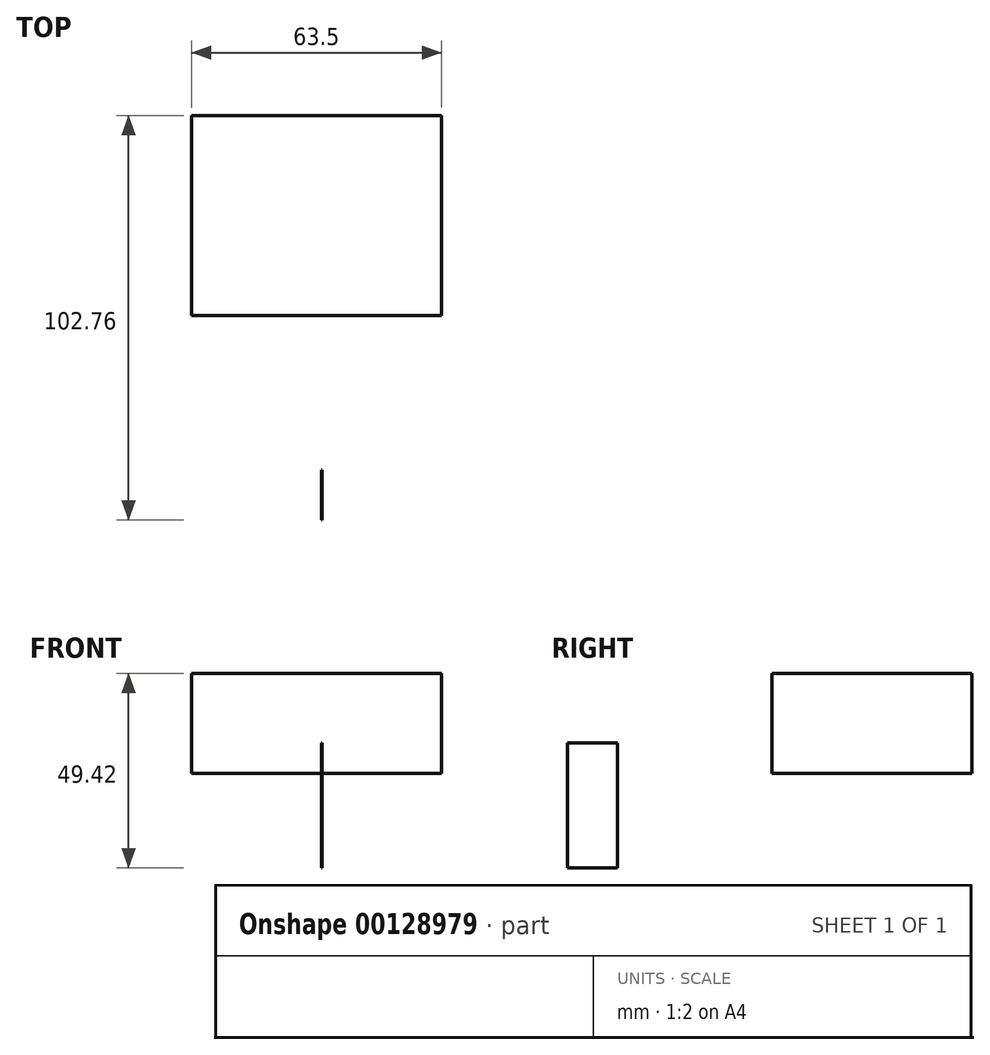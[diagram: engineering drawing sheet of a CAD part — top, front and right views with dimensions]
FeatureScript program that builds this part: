
annotation { "Feature Type Name" : "Feature", "Feature Type Description" : "" }
export const myFeature = defineFeature(function(context is Context, id is Id, definition is map)
    precondition{}
    {
        {
            var Q0;
            Q0=qCreatedBy(makeId("Top.planeOp"),FACE);
            var sketch = newSketch(context, id + "F0", { "sketchPlane" : qUnion([Q0])});
            skLineSegment(sketch, "E0.bottom", {"start": v(-33.07, 30.47) * mm, "end": v(30.43, 30.47) * mm});
            skLineSegment(sketch, "E0.top", {"start": v(-33.07, -20.33) * mm, "end": v(30.43, -20.33) * mm});
            skLineSegment(sketch, "E0.left", {"start": v(-33.07, 30.47) * mm, "end": v(-33.07, -20.33) * mm});
            skLineSegment(sketch, "E0.right", {"start": v(30.43, 30.47) * mm, "end": v(30.43, -20.33) * mm});
            skSolve(sketch);
        }
        {
            var Q0;
            Q0=makeQuery(id+"F0.imprint","IMPRINT",FACE,{"disambiguationData":[TD([[makeQuery(id+"F0.imprint","IMPRINT",EDGE,{"derivedFrom":sQuery(id+"F0.wireOp",EDGE,"E0.bottom")}),-1.0]])]});
            extrude(context, id + "F1", {"entities" : qUnion([Q0]), "depth" : 25.4 * mm});
        }
        {
            var Q0;
            Q0=qCreatedBy(makeId("Right.planeOp"),FACE);
            var sketch = newSketch(context, id + "F2", { "sketchPlane" : qUnion([Q0])});
            skLineSegment(sketch, "E1.bottom", {"start": v(-72.3, 7.73) * mm, "end": v(-59.6, 7.73) * mm});
            skLineSegment(sketch, "E1.top", {"start": v(-72.3, -24.02) * mm, "end": v(-59.6, -24.02) * mm});
            skLineSegment(sketch, "E1.left", {"start": v(-72.3, 7.73) * mm, "end": v(-72.3, -24.02) * mm});
            skLineSegment(sketch, "E1.right", {"start": v(-59.6, 7.73) * mm, "end": v(-59.6, -24.02) * mm});
            skSolve(sketch);
        }
        {
            var Q0;
            Q0=makeQuery(id+"F2.imprint","IMPRINT",FACE,{"disambiguationData":[TD([[makeQuery(id+"F2.imprint","IMPRINT",EDGE,{"derivedFrom":sQuery(id+"F2.wireOp",EDGE,"E1.bottom")}),-1.0]])]});
            extrude(context, id + "F3", {"entities" : qUnion([Q0]), "depth" : 7 / 203.2 * mm});
        }
    });
